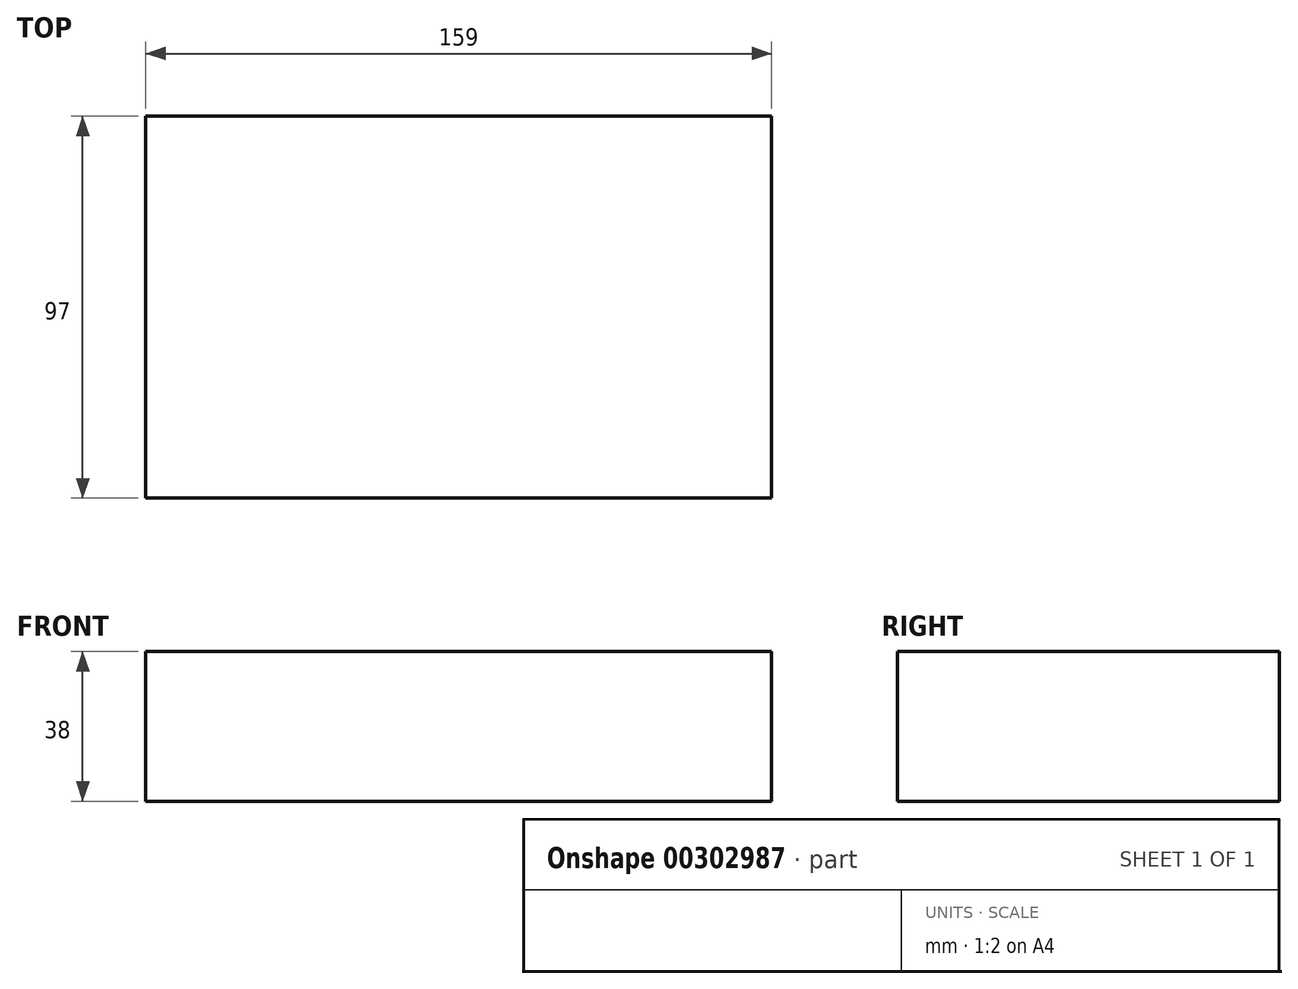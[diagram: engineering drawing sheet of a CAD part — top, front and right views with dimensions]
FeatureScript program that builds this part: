
annotation { "Feature Type Name" : "Feature", "Feature Type Description" : "" }
export const myFeature = defineFeature(function(context is Context, id is Id, definition is map)
    precondition{}
    {
        {
            var Q0;
            Q0=qCreatedBy(makeId("Top.planeOp"),FACE);
            var sketch = newSketch(context, id + "F0", { "sketchPlane" : qUnion([Q0])});
            skLineSegment(sketch, "E0.bottom", {"start": v(-68.25, 50.24) * mm, "end": v(90.75, 50.24) * mm});
            skLineSegment(sketch, "E0.top", {"start": v(-68.25, -46.76) * mm, "end": v(90.75, -46.76) * mm});
            skLineSegment(sketch, "E0.left", {"start": v(-68.25, 50.24) * mm, "end": v(-68.25, -46.76) * mm});
            skLineSegment(sketch, "E0.right", {"start": v(90.75, 50.24) * mm, "end": v(90.75, -46.76) * mm});
            skSolve(sketch);
        }
        {
            var Q0;
            Q0=makeQuery(id+"F0.imprint","IMPRINT",FACE,{"disambiguationData":[TD([[makeQuery(id+"F0.imprint","IMPRINT",EDGE,{"derivedFrom":sQuery(id+"F0.wireOp",EDGE,"E0.bottom")}),-1.0]])]});
            extrude(context, id + "F1", {"entities" : qUnion([Q0]), "depth" : 38 * mm});
        }
    });
